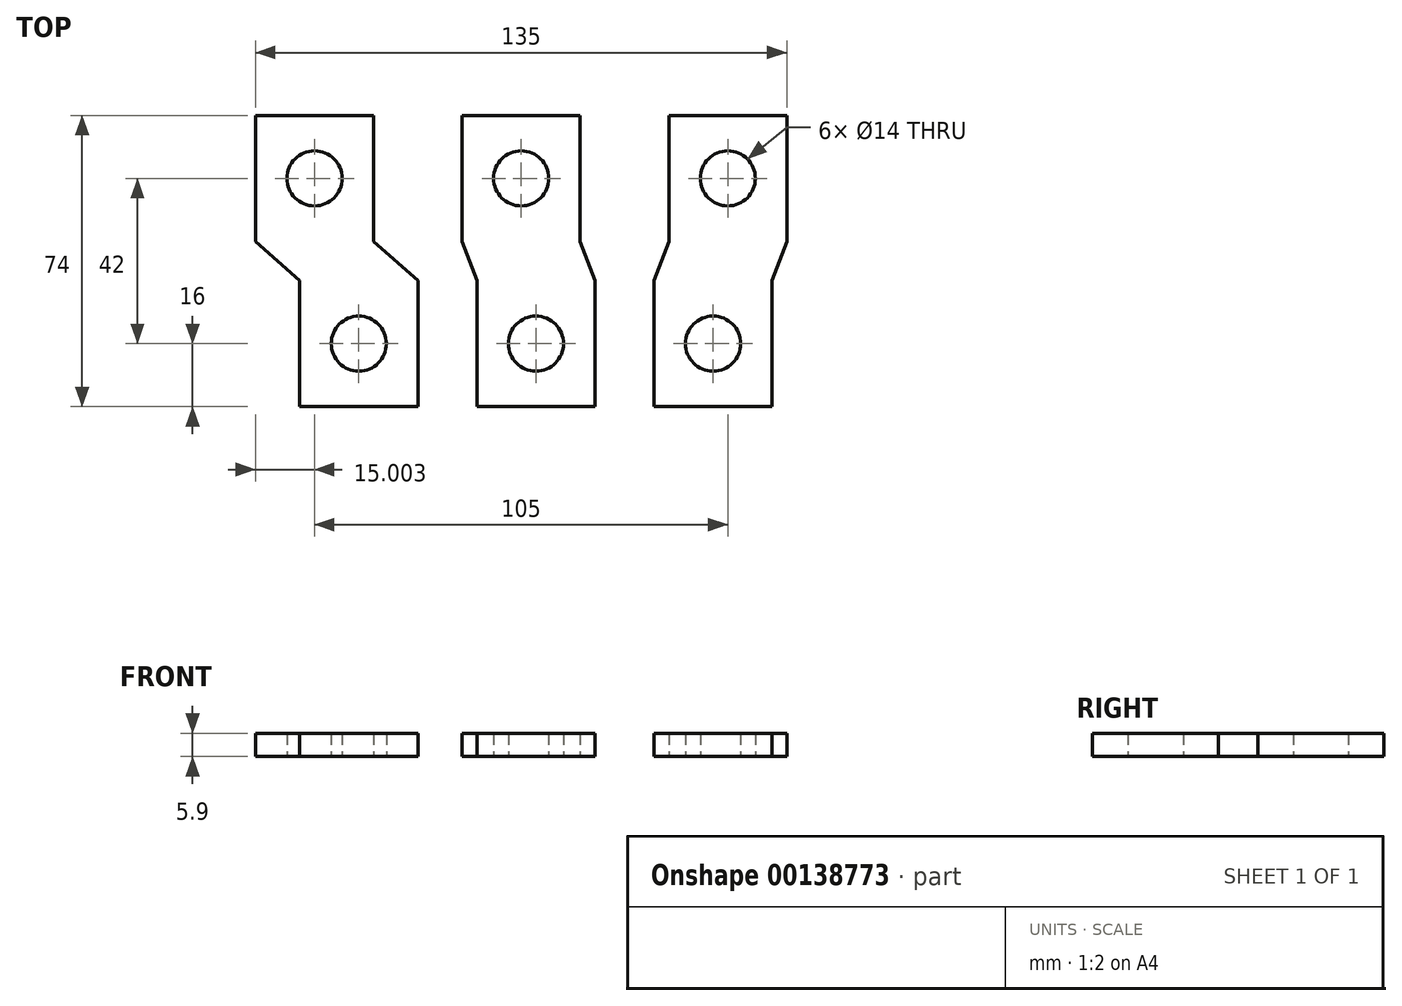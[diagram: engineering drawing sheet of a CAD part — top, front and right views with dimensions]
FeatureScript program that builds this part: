
annotation { "Feature Type Name" : "Feature", "Feature Type Description" : "" }
export const myFeature = defineFeature(function(context is Context, id is Id, definition is map)
    precondition{}
    {
        {
            var Q0;
            Q0=qCreatedBy(makeId("Top.planeOp"),FACE);
            var sketch = newSketch(context, id + "F0", { "sketchPlane" : qUnion([Q0])});
            skLineSegment(sketch, "E0.top", {"start": v(15.84, 37) * mm, "end": v(-14.16, 37) * mm});
            skLineSegment(sketch, "E0.right", {"start": v(-14.16, 5) * mm, "end": v(-14.16, 37) * mm});
            skLineSegment(sketch, "E1.bottom", {"start": v(-36.66, 37) * mm, "end": v(-66.66, 37) * mm});
            skCircle(sketch, "E2", {"center": v(-51.66, 21) * mm, "radius": 7 * mm});
            skLineSegment(sketch, "E3", {"start": v(-55.4, -37) * mm, "end": v(-25.4, -37) * mm});
            skLineSegment(sketch, "E4.left", {"start": v(-25.4, -5) * mm, "end": v(-25.4, -37) * mm});
            skLineSegment(sketch, "E4.right", {"start": v(-55.4, -5) * mm, "end": v(-55.4, -37) * mm});
            skLineSegment(sketch, "E5.left", {"start": v(19.6, -5) * mm, "end": v(19.6, -37) * mm});
            skLineSegment(sketch, "E5.right", {"start": v(-10.4, -5) * mm, "end": v(-10.4, -37) * mm});
            skLineSegment(sketch, "E6", {"start": v(-66.66, 37) * mm, "end": v(-36.66, 37) * mm});
            skLineSegment(sketch, "E7", {"start": v(-55.4, -5) * mm, "end": v(-66.66, 5) * mm});
            skLineSegment(sketch, "E8", {"start": v(-25.4, -5) * mm, "end": v(-36.66, 5) * mm});
            skLineSegment(sketch, "E9", {"start": v(-10.4, -5) * mm, "end": v(-14.16, 5) * mm});
            skLineSegment(sketch, "E10", {"start": v(19.6, -5) * mm, "end": v(15.84, 5) * mm});
            skLineSegment(sketch, "E11", {"start": v(-66.66, 5) * mm, "end": v(-66.66, 37) * mm});
            skLineSegment(sketch, "E12", {"start": v(-36.66, 5) * mm, "end": v(-36.66, 37) * mm});
            skLineSegment(sketch, "E13.trimOffspring", {"start": v(-14.16, 37) * mm, "end": v(15.84, 37) * mm});
            skLineSegment(sketch, "E14.trimOffspring", {"start": v(-10.4, -37) * mm, "end": v(19.6, -37) * mm});
            skLineSegment(sketch, "E15", {"start": v(-40.4, -37) * mm, "end": v(-40.4, -21) * mm});
            skCircle(sketch, "E16", {"center": v(-40.4, -21) * mm, "radius": 7 * mm});
            skCircle(sketch, "E17.1.0.0", {"center": v(4.6, -21) * mm, "radius": 7 * mm});
            skLineSegment(sketch, "E18.trimOffspring", {"start": v(15.84, 5) * mm, "end": v(15.84, 37) * mm});
            skPoint(sketch, "E19", {"position": v(0.84, 37) * mm});
            skPoint(sketch, "E20", {"position": v(-51.66, 37) * mm});
            skPoint(sketch, "E21", {"position": v(0.84, 21) * mm});
            skCircle(sketch, "E22", {"center": v(0.84, 21) * mm, "radius": 7 * mm});
            skLineSegment(sketch, "E23", {"start": v(19.6, -37) * mm, "end": v(34.6, -37) * mm});
            skLineSegment(sketch, "E24", {"start": v(27.1, -37) * mm, "end": v(27.1, -54.96) * mm});
            skLineSegment(sketch, "E25.MirrorCS", {"start": v(90.84, 37) * mm, "end": v(120.84, 37) * mm});
            skLineSegment(sketch, "E26.MirrorCS", {"start": v(38.34, 37) * mm, "end": v(68.34, 37) * mm});
            skLineSegment(sketch, "E27.MirrorCS", {"start": v(64.6, -5) * mm, "end": v(68.34, 5) * mm});
            skLineSegment(sketch, "E28.MirrorCS", {"start": v(120.84, 37) * mm, "end": v(90.84, 37) * mm});
            skLineSegment(sketch, "E29.MirrorCS", {"start": v(64.6, -5) * mm, "end": v(64.6, -37) * mm});
            skLineSegment(sketch, "E30.MirrorCS", {"start": v(34.6, -5) * mm, "end": v(34.6, -37) * mm});
            skCircle(sketch, "E31.MirrorC", {"center": v(105.84, 21) * mm, "radius": 7 * mm});
            skPoint(sketch, "E32.MirrorP", {"position": v(105.84, 37) * mm});
            skCircle(sketch, "E33.MirrorC", {"center": v(53.34, 21) * mm, "radius": 7 * mm});
            skLineSegment(sketch, "E34.MirrorCS", {"start": v(79.6, -5) * mm, "end": v(79.6, -37) * mm});
            skPoint(sketch, "E35.MirrorP", {"position": v(53.34, 37) * mm});
            skLineSegment(sketch, "E36.MirrorCS", {"start": v(109.6, -5) * mm, "end": v(109.6, -37) * mm});
            skLineSegment(sketch, "E37.MirrorCS", {"start": v(109.6, -37) * mm, "end": v(79.6, -37) * mm});
            skLineSegment(sketch, "E38.MirrorCS", {"start": v(68.34, 5) * mm, "end": v(68.34, 37) * mm});
            skLineSegment(sketch, "E39.MirrorCS", {"start": v(90.84, 5) * mm, "end": v(90.84, 37) * mm});
            skLineSegment(sketch, "E40.MirrorCS", {"start": v(120.84, 5) * mm, "end": v(120.84, 37) * mm});
            skLineSegment(sketch, "E41.MirrorCS", {"start": v(94.6, -37) * mm, "end": v(94.6, -21) * mm});
            skLineSegment(sketch, "E42.MirrorCS", {"start": v(64.6, -37) * mm, "end": v(34.6, -37) * mm});
            skLineSegment(sketch, "E43.MirrorCS", {"start": v(34.6, -5) * mm, "end": v(38.34, 5) * mm});
            skCircle(sketch, "E44.MirrorC", {"center": v(94.6, -21) * mm, "radius": 7 * mm});
            skLineSegment(sketch, "E45.MirrorCS", {"start": v(38.34, 5) * mm, "end": v(38.34, 37) * mm});
            skLineSegment(sketch, "E46.MirrorCS", {"start": v(68.34, 37) * mm, "end": v(38.34, 37) * mm});
            skCircle(sketch, "E47.MirrorC", {"center": v(49.6, -21) * mm, "radius": 7 * mm});
            skLineSegment(sketch, "E48.MirrorCS", {"start": v(79.6, -5) * mm, "end": v(90.84, 5) * mm});
            skLineSegment(sketch, "E49.MirrorCS", {"start": v(109.6, -5) * mm, "end": v(120.84, 5) * mm});
            skSolve(sketch);
        }
        {
            var Q0;
            Q0=makeQuery(id+"F0.imprint","IMPRINT",FACE,{"disambiguationData":[TD([[makeQuery(id+"F0.imprint","IMPRINT",EDGE,{"derivedFrom":sQuery(id+"F0.wireOp",EDGE,"E2")}),-1.0]])]});
            var Q1;
            Q1=makeQuery(id+"F0.imprint","IMPRINT",FACE,{"disambiguationData":[TD([[makeQuery(id+"F0.imprint","IMPRINT",EDGE,{"derivedFrom":sQuery(id+"F0.wireOp",EDGE,"E0.right")}),-1.0]])]});
            var Q2;
            Q2=makeQuery(id+"F0.imprint","IMPRINT",FACE,{"disambiguationData":[TD([[makeQuery(id+"F0.imprint","IMPRINT",EDGE,{"derivedFrom":sQuery(id+"F0.wireOp",EDGE,"b8bdfff7-717a-4c1b-ba7f-f7563ed55dac3.MirrorCS")}),-1.0]])]});
            var Q3;
            Q3=makeQuery(id+"F0.imprint","IMPRINT",FACE,{"disambiguationData":[TD([[makeQuery(id+"F0.imprint","IMPRINT",EDGE,{"derivedFrom":sQuery(id+"F0.wireOp",EDGE,"b8bdfff7-717a-4c1b-ba7f-f7563ed55dac2.MirrorCS")}),-1.0]])]});
            var Q4;
            Q4=makeQuery(id+"F0.imprint","IMPRINT",FACE,{"disambiguationData":[TD([[makeQuery(id+"F0.imprint","IMPRINT",EDGE,{"derivedFrom":sQuery(id+"F0.wireOp",EDGE,"E27.MirrorCS")}),1.0]])]});
            var Q5;
            Q5=makeQuery(id+"F0.imprint","IMPRINT",FACE,{"disambiguationData":[TD([[makeQuery(id+"F0.imprint","IMPRINT",EDGE,{"derivedFrom":sQuery(id+"F0.wireOp",EDGE,"E28.MirrorCS")}),1.0]])]});
            extrude(context, id + "F1", {"entities" : qUnion([Q0, Q1, Q2, Q3, Q4, Q5]), "depth" : 5.9 * mm});
        }
    });
